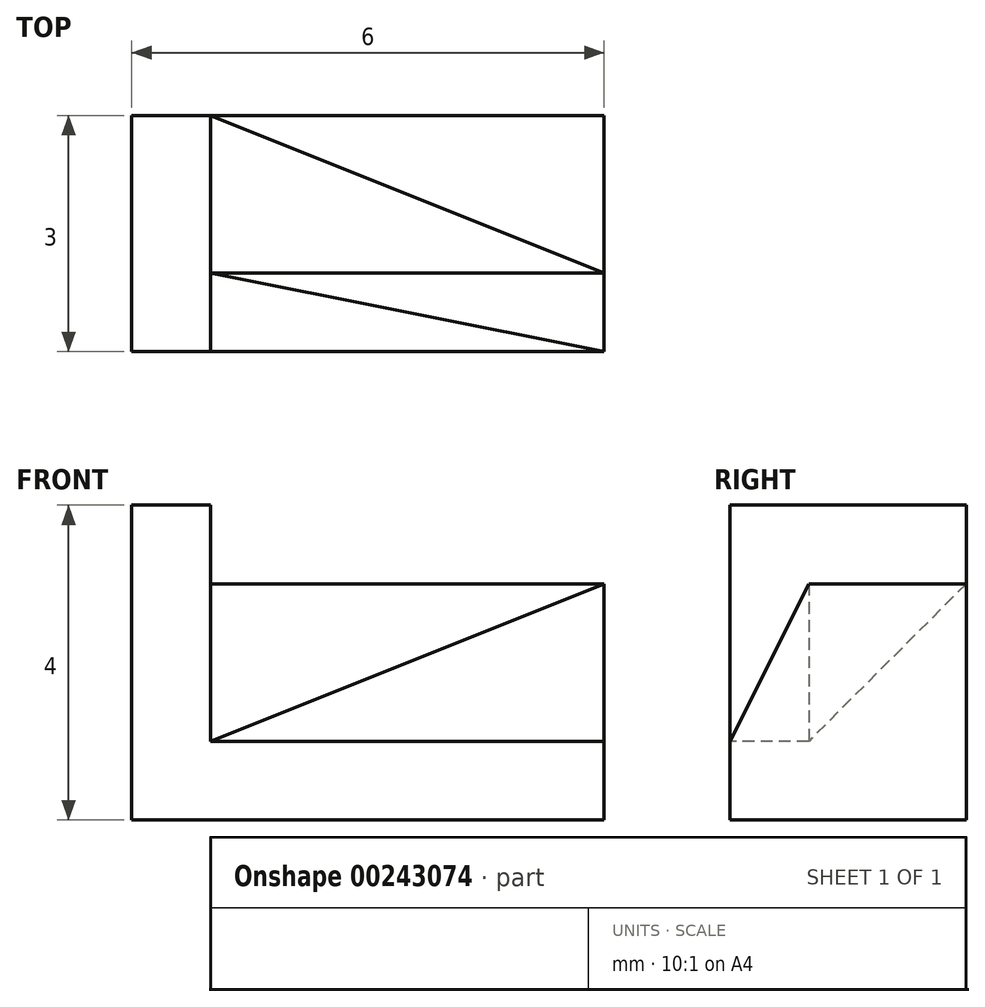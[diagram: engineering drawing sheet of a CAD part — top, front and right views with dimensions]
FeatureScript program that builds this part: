
annotation { "Feature Type Name" : "Feature", "Feature Type Description" : "" }
export const myFeature = defineFeature(function(context is Context, id is Id, definition is map)
    precondition{}
    {
        {
            var Q0;
            Q0=qCreatedBy(makeId("Top.planeOp"),FACE);
            var sketch = newSketch(context, id + "F0", { "sketchPlane" : qUnion([Q0])});
            skLineSegment(sketch, "E0.bottom", {"start": v(0, 0) * mm, "end": v(5, 0) * mm});
            skLineSegment(sketch, "E0.top", {"start": v(0, 3) * mm, "end": v(5, 3) * mm});
            skLineSegment(sketch, "E0.left", {"start": v(0, 0) * mm, "end": v(0, 3) * mm});
            skLineSegment(sketch, "E0.right", {"start": v(5, 0) * mm, "end": v(5, 3) * mm});
            skSolve(sketch);
        }
        {
            var Q0;
            Q0=makeQuery(id+"F0.imprint","IMPRINT",FACE,{"disambiguationData":[TD([[makeQuery(id+"F0.imprint","IMPRINT",EDGE,{"derivedFrom":sQuery(id+"F0.wireOp",EDGE,"E0.bottom")}),1.0]])]});
            extrude(context, id + "F1", {"entities" : qUnion([Q0]), "depth" : 3 * mm});
        }
        {
            var Q0;
            Q0=makeQuery(id+"F1.opExtrude","CAP_FACE",FACE,{"disambiguationData":[OSD([sQuery(id+"F0.wireOp",EDGE,"E0.bottom"),sQuery(id+"F0.wireOp",EDGE,"E0.top"),sQuery(id+"F0.wireOp",EDGE,"E0.left"),sQuery(id+"F0.wireOp",EDGE,"E0.right")])],"isStart":false});
            var sketch = newSketch(context, id + "F2", { "sketchPlane" : qUnion([Q0])});
            skLineSegment(sketch, "E1", {"start": v(0, 0) * mm, "end": v(0, 1) * mm});
            skLineSegment(sketch, "E2", {"start": v(0, 1) * mm, "end": v(5, 0) * mm});
            skLineSegment(sketch, "E3", {"start": v(5, 0) * mm, "end": v(0, 0) * mm});
            skSolve(sketch);
        }
        {
            var Q0;
            Q0 = qSketchRegion(id + "F2", true);
            var Q1;
            Q1=makeQuery(id+"F2.imprint","IMPRINT",FACE,{"disambiguationData":[TD([[makeQuery(id+"F2.imprint","IMPRINT",EDGE,{"derivedFrom":sQuery(id+"F2.wireOp",EDGE,"E1")}),-1.0]])]});
            extrude(context, id + "F3", {"entities" : qUnion([Q0, Q1]), "operationType" : NewBodyOperationType.REMOVE, "oppositeDirection" : true, "depth" : 2 * mm});
        }
        {
            var Q0;
            Q0=makeQuery(id+"F1.opExtrude","SWEPT_FACE",FACE,{"disambiguationData":[OSD([sQuery(id+"F0.wireOp",EDGE,"E0.right")])]});
            var sketch = newSketch(context, id + "F4", { "sketchPlane" : qUnion([Q0])});
            skLineSegment(sketch, "E4", {"start": v(0, 3) * mm, "end": v(1, 3) * mm});
            skSolve(sketch);
        }
        {
            var Q0;
            Q0=makeQuery(id+"F3.boolean.opBoolean","COPY",VERTEX,{"derivedFrom":makeQuery(id+"F3.opExtrude","CAP_VERTEX",VERTEX,{"disambiguationData":[OSD([sQuery(id+"F0.wireOp",EDGE,"E0.left"),sQuery(id+"F2.wireOp",EDGE,"E1"),sQuery(id+"F2.wireOp",EDGE,"E2")])],"isStart":false})});
            var Q1;
            Q1=makeQuery(id+"F3.boolean.opBoolean","COPY",VERTEX,{"derivedFrom":makeQuery(id+"F3.opExtrude","CAP_VERTEX",VERTEX,{"disambiguationData":[OSD([sQuery(id+"F0.wireOp",EDGE,"E0.right"),sQuery(id+"F2.wireOp",EDGE,"E2"),sQuery(id+"F2.wireOp",EDGE,"E3")])],"isStart":false})});
            var Q2;
            Q2=sQuery(id+"F4.wireOp",VERTEX,"E4.end");
            cPlane(context, id + "F5", {"entities" : qUnion([Q0, Q1, Q2]), "cplaneType" : CPlaneType.THREE_POINT, "offset" : 25 * mm, "width" : 150 * mm, "height" : 150 * mm});
        }
        {
            var Q0;
            Q0=qCreatedBy(id+"F5.planeOp",FACE);
            var sketch = newSketch(context, id + "F6", { "sketchPlane" : qUnion([Q0])});
            skPoint(sketch, "E5.0", {"position": v(-5, 0.9) * mm});
            skPoint(sketch, "E5.1", {"position": v(-5, 3.13) * mm});
            skPoint(sketch, "E5.2", {"position": v(-0.08, 3.13) * mm});
            skPoint(sketch, "E6.0", {"position": v(0.08, 1.34) * mm});
            skLineSegment(sketch, "E7", {"start": v(-5, 0.9) * mm, "end": v(0.08, 1.34) * mm});
            skPoint(sketch, "E8.0", {"position": v(0.08, 3.58) * mm});
            skLineSegment(sketch, "E9", {"start": v(0.08, 1.34) * mm, "end": v(0.08, 3.58) * mm});
            skLineSegment(sketch, "E10", {"start": v(0.08, 3.58) * mm, "end": v(-5, 3.13) * mm});
            skLineSegment(sketch, "E11", {"start": v(-5, 3.13) * mm, "end": v(-5.97, 3.05) * mm});
            skLineSegment(sketch, "E12", {"start": v(-5.97, 3.05) * mm, "end": v(-5, 0.9) * mm});
            skSolve(sketch);
        }
        {
            var Q0;
            Q0=makeQuery(id+"F6.imprint","IMPRINT",FACE,{"disambiguationData":[TD([[makeQuery(id+"F6.imprint","IMPRINT",EDGE,{"derivedFrom":sQuery(id+"F6.wireOp",EDGE,"E7")}),1.0]])]});
            extrude(context, id + "F7", {"entities" : qUnion([Q0]), "operationType" : NewBodyOperationType.REMOVE, "oppositeDirection" : true, "depth" : 25 * mm});
        }
        {
            var Q0;
            Q0=makeQuery(id+"F1.opExtrude","CAP_VERTEX",VERTEX,{"disambiguationData":[OSD([sQuery(id+"F0.wireOp",EDGE,"E0.top"),sQuery(id+"F0.wireOp",EDGE,"E0.left")])],"isStart":false});
            var Q1;
            Q1=makeQuery(id+"F7.boolean.opBoolean","MERGE",VERTEX,{"derivedFrom":[makeQuery(id+"F3.boolean.opBoolean","COPY",VERTEX,{"derivedFrom":makeQuery(id+"F3.opExtrude","CAP_VERTEX",VERTEX,{"disambiguationData":[OSD([sQuery(id+"F0.wireOp",EDGE,"E0.left"),sQuery(id+"F2.wireOp",EDGE,"E1"),sQuery(id+"F2.wireOp",EDGE,"E2")])],"isStart":false})}),makeQuery(id+"F7.opExtrude","CAP_VERTEX",VERTEX,{"disambiguationData":[OSD([sQuery(id+"F6.wireOp",EDGE,"E7"),sQuery(id+"F6.wireOp",EDGE,"E9")])],"isStart":true})]});
            var Q2;
            Q2=sQuery(id+"F4.wireOp",VERTEX,"E4.end");
            cPlane(context, id + "F8", {"entities" : qUnion([Q0, Q1, Q2]), "cplaneType" : CPlaneType.THREE_POINT, "offset" : 25 * mm, "width" : 150 * mm, "height" : 150 * mm});
        }
        {
            var Q0;
            Q0=qCreatedBy(id+"F8.planeOp",FACE);
            var sketch = newSketch(context, id + "F9", { "sketchPlane" : qUnion([Q0])});
            skPoint(sketch, "E13.0", {"position": v(0, 4.24) * mm});
            skPoint(sketch, "E13.1", {"position": v(0, 1.41) * mm});
            skPoint(sketch, "E13.2", {"position": v(-5.2, 2.83) * mm});
            skLineSegment(sketch, "E14", {"start": v(-5.2, 2.83) * mm, "end": v(0, 1.41) * mm});
            skLineSegment(sketch, "E15", {"start": v(0, 4.24) * mm, "end": v(-5.2, 2.83) * mm});
            skLineSegment(sketch, "E16", {"start": v(0, 4.24) * mm, "end": v(0.58, 4.4) * mm});
            skLineSegment(sketch, "E17", {"start": v(0.58, 4.4) * mm, "end": v(0, 1.41) * mm});
            skSolve(sketch);
        }
        {
            var Q0;
            Q0=makeQuery(id+"F9.imprint","IMPRINT",FACE,{"disambiguationData":[TD([[makeQuery(id+"F9.imprint","IMPRINT",EDGE,{"derivedFrom":sQuery(id+"F9.wireOp",EDGE,"E14")}),1.0]])]});
            extrude(context, id + "F10", {"entities" : qUnion([Q0]), "operationType" : NewBodyOperationType.REMOVE, "oppositeDirection" : true, "depth" : 25 * mm});
        }
        {
            var Q0;
            Q0=makeQuery(id+"F1.opExtrude","SWEPT_FACE",FACE,{"disambiguationData":[OSD([sQuery(id+"F0.wireOp",EDGE,"E0.left")])]});
            var sketch = newSketch(context, id + "F11", { "sketchPlane" : qUnion([Q0])});
            skLineSegment(sketch, "E18.bottom", {"start": v(-3, 0) * mm, "end": v(0, 0) * mm});
            skLineSegment(sketch, "E18.top", {"start": v(-3, 4) * mm, "end": v(0, 4) * mm});
            skLineSegment(sketch, "E18.left", {"start": v(-3, 0) * mm, "end": v(-3, 4) * mm});
            skLineSegment(sketch, "E18.right", {"start": v(0, 0) * mm, "end": v(0, 4) * mm});
            skSolve(sketch);
        }
        {
            var Q0;
            Q0 = qSketchRegion(id + "F11", true);
            extrude(context, id + "F12", {"entities" : qUnion([Q0]), "operationType" : NewBodyOperationType.ADD, "depth" : 1 * mm});
        }
    });
